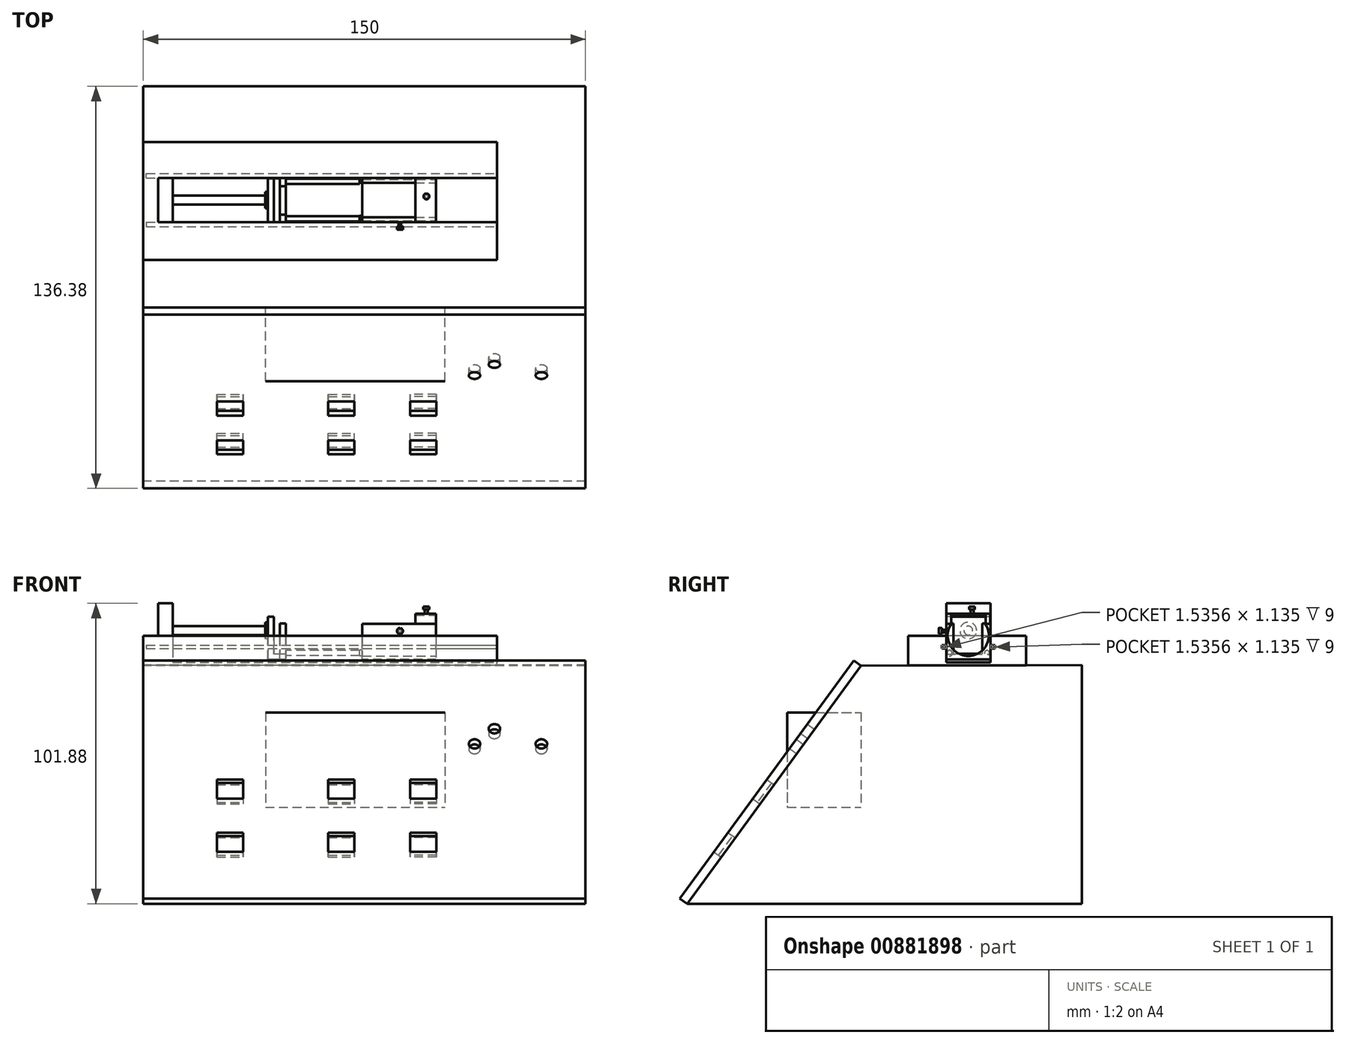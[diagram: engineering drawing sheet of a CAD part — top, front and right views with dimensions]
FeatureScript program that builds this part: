
annotation { "Feature Type Name" : "Feature", "Feature Type Description" : "" }
export const myFeature = defineFeature(function(context is Context, id is Id, definition is map)
    precondition{}
    {
        {
            var Q0;
            Q0=qCreatedBy(makeId("Right.planeOp"),FACE);
            var sketch = newSketch(context, id + "F0", { "sketchPlane" : qUnion([Q0])});
            skLineSegment(sketch, "E0", {"start": v(0, 80.75) * mm, "end": v(-58.99, 0) * mm});
            skLineSegment(sketch, "E1", {"start": v(-58.99, 0) * mm, "end": v(74.97, 0) * mm});
            skLineSegment(sketch, "E2", {"start": v(74.97, 0) * mm, "end": v(74.97, 80.92) * mm});
            skLineSegment(sketch, "E3", {"start": v(74.97, 80.92) * mm, "end": v(0, 80.75) * mm});
            skSolve(sketch);
        }
        {
            var Q0;
            Q0 = qSketchRegion(id + "F0", true);
            extrude(context, id + "F1", {"entities" : qUnion([Q0]), "depth" : 150 * mm, "offsetDistance" : 25 * mm});
        }
        {
            var Q0;
            Q0=makeQuery(id+"F1.opExtrude","CAP_FACE",FACE,{"disambiguationData":[OSD([sQuery(id+"F0.wireOp",EDGE,"E0"),sQuery(id+"F0.wireOp",EDGE,"E1"),sQuery(id+"F0.wireOp",EDGE,"E2"),sQuery(id+"F0.wireOp",EDGE,"E3")])],"isStart":true});
            var sketch = newSketch(context, id + "F2", { "sketchPlane" : qUnion([Q0])});
            skLineSegment(sketch, "E4.bottom", {"start": v(-56.05, 80.88) * mm, "end": v(-16.05, 80.88) * mm});
            skLineSegment(sketch, "E4.top", {"start": v(-56.05, 90.88) * mm, "end": v(-16.05, 90.88) * mm});
            skLineSegment(sketch, "E4.left", {"start": v(-56.05, 80.88) * mm, "end": v(-56.05, 90.88) * mm});
            skLineSegment(sketch, "E4.right", {"start": v(-16.05, 80.88) * mm, "end": v(-16.05, 90.88) * mm});
            skSolve(sketch);
        }
        {
            var Q0;
            Q0 = qSketchRegion(id + "F2", true);
            extrude(context, id + "F3", {"entities" : qUnion([Q0]), "oppositeDirection" : true, "depth" : 120 * mm, "offsetDistance" : 25 * mm});
        }
        {
            var Q0;
            Q0=makeQuery(id+"F3.opExtrude","CAP_FACE",FACE,{"disambiguationData":[OSD([sQuery(id+"F2.wireOp",EDGE,"E4.bottom"),sQuery(id+"F2.wireOp",EDGE,"E4.top"),sQuery(id+"F2.wireOp",EDGE,"E4.left"),sQuery(id+"F2.wireOp",EDGE,"E4.right")])],"isStart":false});
            var sketch = newSketch(context, id + "F4", { "sketchPlane" : qUnion([Q0])});
            skLineSegment(sketch, "E5.bottom", {"start": v(28.9, 90.88) * mm, "end": v(43.9, 90.88) * mm});
            skLineSegment(sketch, "E5.top", {"start": v(28.9, 81.88) * mm, "end": v(43.9, 81.88) * mm});
            skLineSegment(sketch, "E5.left", {"start": v(28.9, 90.88) * mm, "end": v(28.9, 81.88) * mm});
            skLineSegment(sketch, "E5.right", {"start": v(43.9, 90.88) * mm, "end": v(43.9, 81.88) * mm});
            skSolve(sketch);
        }
        {
            var Q0;
            Q0 = qSketchRegion(id + "F4", true);
            extrude(context, id + "F5", {"entities" : qUnion([Q0]), "operationType" : NewBodyOperationType.REMOVE, "oppositeDirection" : true, "depth" : 115 * mm, "offsetDistance" : 25 * mm});
        }
        {
            var Q0;
            Q0=makeQuery(id+"F5.boolean.opBoolean","COPY",FACE,{"derivedFrom":makeQuery(id+"F5.opExtrude","CAP_FACE",FACE,{"disambiguationData":[OSD([sQuery(id+"F4.wireOp",EDGE,"E5.bottom"),sQuery(id+"F4.wireOp",EDGE,"E5.top"),sQuery(id+"F4.wireOp",EDGE,"E5.left"),sQuery(id+"F4.wireOp",EDGE,"E5.right")])],"isStart":false})});
            var sketch = newSketch(context, id + "F6", { "sketchPlane" : qUnion([Q0])});
            skLineSegment(sketch, "E6.bottom", {"start": v(28.9, 81.88) * mm, "end": v(43.9, 81.88) * mm});
            skLineSegment(sketch, "E6.top", {"start": v(28.9, 101.88) * mm, "end": v(43.9, 101.88) * mm});
            skLineSegment(sketch, "E6.left", {"start": v(28.9, 81.88) * mm, "end": v(28.9, 101.88) * mm});
            skLineSegment(sketch, "E6.right", {"start": v(43.9, 81.88) * mm, "end": v(43.9, 101.88) * mm});
            skSolve(sketch);
        }
        {
            var Q0;
            Q0 = qSketchRegion(id + "F6", true);
            extrude(context, id + "F7", {"entities" : qUnion([Q0]), "operationType" : NewBodyOperationType.ADD, "depth" : 5 * mm, "offsetDistance" : 25 * mm});
        }
        {
            var Q0;
            Q0=makeQuery(id+"F7.opExtrude","CAP_FACE",FACE,{"disambiguationData":[OSD([sQuery(id+"F6.wireOp",EDGE,"E6.bottom"),sQuery(id+"F6.wireOp",EDGE,"E6.top"),sQuery(id+"F6.wireOp",EDGE,"E6.left"),sQuery(id+"F6.wireOp",EDGE,"E6.right")])],"isStart":false});
            var sketch = newSketch(context, id + "F8", { "sketchPlane" : qUnion([Q0])});
            skCircle(sketch, "E7", {"center": v(36.4, 92.68) * mm, "radius": 1.5 * mm});
            skSolve(sketch);
        }
        {
            var Q0;
            Q0 = qSketchRegion(id + "F8", true);
            extrude(context, id + "F9", {"entities" : qUnion([Q0]), "operationType" : NewBodyOperationType.ADD, "depth" : 31.3 * mm, "offsetDistance" : 25 * mm});
        }
        {
            var Q0;
            Q0=makeQuery(id+"F9.opExtrude","CAP_FACE",FACE,{"disambiguationData":[OSD([sQuery(id+"F8.wireOp",EDGE,"E7")])],"isStart":false});
            var sketch = newSketch(context, id + "F10", { "sketchPlane" : qUnion([Q0])});
            skCircle(sketch, "E8", {"center": v(36.4, 92.68) * mm, "radius": 2.83 * mm});
            skSolve(sketch);
        }
        {
            var Q0;
            Q0 = qSketchRegion(id + "F10", true);
            extrude(context, id + "F11", {"entities" : qUnion([Q0]), "operationType" : NewBodyOperationType.ADD, "depth" : 1 * mm, "offsetDistance" : 25 * mm});
        }
        {
            var Q0;
            Q0=makeQuery(id+"F11.opExtrude","CAP_FACE",FACE,{"disambiguationData":[OSD([sQuery(id+"F10.wireOp",EDGE,"E8")])],"isStart":false});
            var sketch = newSketch(context, id + "F12", { "sketchPlane" : qUnion([Q0])});
            skLineSegment(sketch, "E9", {"start": v(28.96, 82.93) * mm, "end": v(43.82, 82.93) * mm});
            skLineSegment(sketch, "E10", {"start": v(43.82, 82.93) * mm, "end": v(43.82, 97.32) * mm});
            skLineSegment(sketch, "E11", {"start": v(43.82, 97.32) * mm, "end": v(28.96, 97.32) * mm});
            skLineSegment(sketch, "E12", {"start": v(28.96, 97.32) * mm, "end": v(28.96, 82.93) * mm});
            skSolve(sketch);
        }
        {
            var Q0;
            Q0 = qSketchRegion(id + "F12", true);
            extrude(context, id + "F13", {"entities" : qUnion([Q0]), "operationType" : NewBodyOperationType.ADD, "depth" : 2 * mm, "offsetDistance" : 25 * mm});
        }
        {
            var Q0;
            Q0=makeQuery(id+"F13.opExtrude","CAP_FACE",FACE,{"disambiguationData":[OSD([sQuery(id+"F12.wireOp",EDGE,"E9"),sQuery(id+"F12.wireOp",EDGE,"E10"),sQuery(id+"F12.wireOp",EDGE,"E11"),sQuery(id+"F12.wireOp",EDGE,"E12")])],"isStart":false});
            var sketch = newSketch(context, id + "F14", { "sketchPlane" : qUnion([Q0])});
            skLineSegment(sketch, "E13.bottom", {"start": v(28.96, 82.93) * mm, "end": v(43.82, 82.93) * mm});
            skLineSegment(sketch, "E13.top", {"start": v(28.96, 84.65) * mm, "end": v(43.82, 84.65) * mm});
            skLineSegment(sketch, "E13.left", {"start": v(28.96, 82.93) * mm, "end": v(28.96, 84.65) * mm});
            skLineSegment(sketch, "E13.right", {"start": v(43.82, 82.93) * mm, "end": v(43.82, 84.65) * mm});
            skSolve(sketch);
        }
        {
            var Q0;
            Q0=makeQuery(id+"F14.imprint","IMPRINT",FACE,{"disambiguationData":[TD([[makeQuery(id+"F14.imprint","IMPRINT",EDGE,{"derivedFrom":sQuery(id+"F14.wireOp",EDGE,"E13.bottom")}),1.0]])]});
            extrude(context, id + "F15", {"entities" : qUnion([Q0]), "operationType" : NewBodyOperationType.ADD, "depth" : 2 * mm, "offsetDistance" : 25 * mm});
        }
        {
            var Q0;
            Q0=makeQuery(id+"F15.opExtrude","CAP_FACE",FACE,{"disambiguationData":[OSD([sQuery(id+"F14.wireOp",EDGE,"E13.bottom"),sQuery(id+"F14.wireOp",EDGE,"E13.top"),sQuery(id+"F14.wireOp",EDGE,"E13.left"),sQuery(id+"F14.wireOp",EDGE,"E13.right")])],"isStart":false});
            var sketch = newSketch(context, id + "F16", { "sketchPlane" : qUnion([Q0])});
            skLineSegment(sketch, "E14.bottom", {"start": v(28.96, 82.93) * mm, "end": v(43.85, 82.93) * mm});
            skLineSegment(sketch, "E14.top", {"start": v(28.96, 95.1) * mm, "end": v(43.85, 95.1) * mm});
            skLineSegment(sketch, "E14.left", {"start": v(28.96, 82.93) * mm, "end": v(28.96, 95.1) * mm});
            skLineSegment(sketch, "E14.right", {"start": v(43.85, 82.93) * mm, "end": v(43.85, 95.1) * mm});
            skSolve(sketch);
        }
        {
            var Q0;
            Q0 = qSketchRegion(id + "F16", true);
            extrude(context, id + "F17", {"entities" : qUnion([Q0]), "operationType" : NewBodyOperationType.ADD, "depth" : 2 * mm, "offsetDistance" : 25 * mm});
        }
        {
            var Q0;
            Q0=makeQuery(id+"F17.opExtrude","CAP_FACE",FACE,{"disambiguationData":[OSD([sQuery(id+"F16.wireOp",EDGE,"E14.bottom"),sQuery(id+"F16.wireOp",EDGE,"E14.top"),sQuery(id+"F16.wireOp",EDGE,"E14.left"),sQuery(id+"F16.wireOp",EDGE,"E14.right")])],"isStart":false});
            var sketch = newSketch(context, id + "F18", { "sketchPlane" : qUnion([Q0])});
            skLineSegment(sketch, "E15.bottom", {"start": v(31.42, 95.1) * mm, "end": v(41.14, 95.1) * mm});
            skLineSegment(sketch, "E15.top", {"start": v(31.42, 84.76) * mm, "end": v(41.14, 84.76) * mm});
            skLineSegment(sketch, "E15.left", {"start": v(31.42, 95.1) * mm, "end": v(31.42, 84.76) * mm});
            skLineSegment(sketch, "E15.right", {"start": v(41.14, 95.1) * mm, "end": v(41.14, 84.76) * mm});
            skSolve(sketch);
        }
        {
            var Q0;
            Q0 = qSketchRegion(id + "F18", true);
            extrude(context, id + "F19", {"entities" : qUnion([Q0]), "operationType" : NewBodyOperationType.REMOVE, "oppositeDirection" : true, "depth" : 2 * mm, "offsetDistance" : 25 * mm});
        }
        {
            var Q0;
            Q0=makeQuery(id+"F3.opExtrude","CAP_FACE",FACE,{"disambiguationData":[OSD([sQuery(id+"F2.wireOp",EDGE,"E4.bottom"),sQuery(id+"F2.wireOp",EDGE,"E4.top"),sQuery(id+"F2.wireOp",EDGE,"E4.left"),sQuery(id+"F2.wireOp",EDGE,"E4.right")])],"isStart":false});
            var sketch = newSketch(context, id + "F20", { "sketchPlane" : qUnion([Q0])});
            skLineSegment(sketch, "E16.bottom", {"start": v(43.9, 87.7) * mm, "end": v(45.44, 87.7) * mm});
            skLineSegment(sketch, "E16.top", {"start": v(43.9, 86.56) * mm, "end": v(45.44, 86.56) * mm});
            skLineSegment(sketch, "E16.left", {"start": v(43.9, 87.7) * mm, "end": v(43.9, 86.56) * mm});
            skLineSegment(sketch, "E16.right", {"start": v(45.44, 87.7) * mm, "end": v(45.44, 86.56) * mm});
            skLineSegment(sketch, "E17", {"start": v(36.4, 81.88) * mm, "end": v(36.4, 97.63) * mm});
            skLineSegment(sketch, "E18.MirrorCS", {"start": v(28.9, 87.7) * mm, "end": v(27.37, 87.7) * mm});
            skLineSegment(sketch, "E19.MirrorCS", {"start": v(27.37, 87.7) * mm, "end": v(27.37, 86.56) * mm});
            skLineSegment(sketch, "E20.MirrorCS", {"start": v(28.9, 86.56) * mm, "end": v(27.37, 86.56) * mm});
            skLineSegment(sketch, "E21.MirrorCS", {"start": v(28.9, 87.7) * mm, "end": v(28.9, 86.56) * mm});
            skSolve(sketch);
        }
        {
            var Q0;
            Q0=makeQuery(id+"F20.imprint","IMPRINT",FACE,{"disambiguationData":[TD([[makeQuery(id+"F20.imprint","IMPRINT",EDGE,{"derivedFrom":sQuery(id+"F20.wireOp",EDGE,"E16.bottom")}),-1.0]])]});
            var Q1;
            Q1=makeQuery(id+"F20.imprint","IMPRINT",FACE,{"disambiguationData":[TD([[makeQuery(id+"F20.imprint","IMPRINT",EDGE,{"derivedFrom":sQuery(id+"F20.wireOp",EDGE,"E18.MirrorCS")}),1.0]])]});
            extrude(context, id + "F21", {"entities" : qUnion([Q0, Q1]), "operationType" : NewBodyOperationType.REMOVE, "oppositeDirection" : true, "depth" : 119 * mm, "offsetDistance" : 25 * mm});
        }
        {
            var Q0;
            Q0=qCreatedBy(makeId("Front.planeOp"),FACE);
            var sketch = newSketch(context, id + "F22", { "sketchPlane" : qUnion([Q0])});
            skLineSegment(sketch, "E22.bottom", {"start": v(41.44, 64.84) * mm, "end": v(102.33, 64.84) * mm});
            skLineSegment(sketch, "E22.top", {"start": v(41.44, 32.77) * mm, "end": v(102.33, 32.77) * mm});
            skLineSegment(sketch, "E22.left", {"start": v(41.44, 64.84) * mm, "end": v(41.44, 32.77) * mm});
            skLineSegment(sketch, "E22.right", {"start": v(102.33, 64.84) * mm, "end": v(102.33, 32.77) * mm});
            skSolve(sketch);
        }
        {
            var Q0;
            Q0 = qSketchRegion(id + "F22", true);
            extrude(context, id + "F23", {"entities" : qUnion([Q0]), "depth" : 25 * mm, "offsetDistance" : 25 * mm});
        }
        {
            var Q0;
            Q0=makeQuery(id+"F1.opExtrude","SWEPT_FACE",FACE,{"disambiguationData":[OSD([sQuery(id+"F0.wireOp",EDGE,"E0")])]});
            var sketch = newSketch(context, id + "F24", { "sketchPlane" : qUnion([Q0])});
            skPoint(sketch, "E23.firstSnap0", {"position": v(0, 15.2) * mm});
            skLineSegment(sketch, "E23.bottom", {"start": v(24.95, 15.2) * mm, "end": v(33.86, 15.2) * mm});
            skLineSegment(sketch, "E23.top", {"start": v(24.95, 7.09) * mm, "end": v(33.86, 7.09) * mm});
            skLineSegment(sketch, "E23.left", {"start": v(24.95, 15.2) * mm, "end": v(24.95, 7.09) * mm});
            skLineSegment(sketch, "E23.right", {"start": v(33.86, 15.2) * mm, "end": v(33.86, 7.09) * mm});
            skLineSegment(sketch, "E24.MirrorCS", {"start": v(24.95, -15.2) * mm, "end": v(33.86, -15.2) * mm});
            skLineSegment(sketch, "E25.MirrorCS", {"start": v(24.95, -15.2) * mm, "end": v(24.95, -7.09) * mm});
            skLineSegment(sketch, "E26.MirrorCS", {"start": v(24.95, -7.09) * mm, "end": v(33.86, -7.09) * mm});
            skLineSegment(sketch, "E27.MirrorCS", {"start": v(33.86, -15.2) * mm, "end": v(33.86, -7.09) * mm});
            skLineSegment(sketch, "E28.MirrorCS", {"start": v(99.45, 15.2) * mm, "end": v(90.54, 15.2) * mm});
            skLineSegment(sketch, "E29.MirrorCS", {"start": v(99.45, 15.2) * mm, "end": v(99.45, 7.09) * mm});
            skLineSegment(sketch, "E30.MirrorCS", {"start": v(99.45, 7.09) * mm, "end": v(90.54, 7.09) * mm});
            skLineSegment(sketch, "E31.MirrorCS", {"start": v(90.54, 15.2) * mm, "end": v(90.54, 7.09) * mm});
            skLineSegment(sketch, "E32.MirrorCS", {"start": v(99.45, -7.09) * mm, "end": v(90.54, -7.09) * mm});
            skLineSegment(sketch, "E33.MirrorCS", {"start": v(99.45, -15.2) * mm, "end": v(99.45, -7.09) * mm});
            skLineSegment(sketch, "E34.MirrorCS", {"start": v(99.45, -15.2) * mm, "end": v(90.54, -15.2) * mm});
            skLineSegment(sketch, "E35.MirrorCS", {"start": v(90.54, -15.2) * mm, "end": v(90.54, -7.09) * mm});
            skLineSegment(sketch, "E36.MirrorCS", {"start": v(62.74, 15.2) * mm, "end": v(71.65, 15.2) * mm});
            skLineSegment(sketch, "E37.MirrorCS", {"start": v(71.65, 15.2) * mm, "end": v(71.65, 7.09) * mm});
            skLineSegment(sketch, "E38.MirrorCS", {"start": v(62.74, 7.09) * mm, "end": v(71.65, 7.09) * mm});
            skLineSegment(sketch, "E39.MirrorCS", {"start": v(62.74, 15.2) * mm, "end": v(62.74, 7.09) * mm});
            skLineSegment(sketch, "E40.MirrorCS", {"start": v(62.74, -7.09) * mm, "end": v(71.65, -7.09) * mm});
            skLineSegment(sketch, "E41.MirrorCS", {"start": v(71.65, -15.2) * mm, "end": v(71.65, -7.09) * mm});
            skLineSegment(sketch, "E42.MirrorCS", {"start": v(62.74, -15.2) * mm, "end": v(62.74, -7.09) * mm});
            skLineSegment(sketch, "E43.MirrorCS", {"start": v(62.74, -15.2) * mm, "end": v(71.65, -15.2) * mm});
            skCircle(sketch, "E44", {"center": v(112.34, 36.51) * mm, "radius": 1.95 * mm});
            skCircle(sketch, "E45.MirrorC", {"center": v(112.34, 30.16) * mm, "radius": 1.95 * mm});
            skCircle(sketch, "E46.MirrorC", {"center": v(119.08, 36.51) * mm, "radius": 1.95 * mm});
            skCircle(sketch, "E47.MirrorC", {"center": v(119.08, 30.16) * mm, "radius": 1.95 * mm});
            skCircle(sketch, "E48.MirrorC", {"center": v(135.01, 36.51) * mm, "radius": 1.95 * mm});
            skCircle(sketch, "E49.MirrorC", {"center": v(135.01, 30.16) * mm, "radius": 1.95 * mm});
            skSolve(sketch);
        }
        {
            var Q0;
            Q0=makeQuery(id+"F24.imprint","IMPRINT",FACE,{"disambiguationData":[TD([[makeQuery(id+"F24.imprint","IMPRINT",EDGE,{"derivedFrom":sQuery(id+"F24.wireOp",EDGE,"E23.bottom")}),-1.0]])]});
            var Q1;
            Q1=makeQuery(id+"F24.imprint","IMPRINT",FACE,{"disambiguationData":[TD([[makeQuery(id+"F24.imprint","IMPRINT",EDGE,{"derivedFrom":sQuery(id+"F24.wireOp",EDGE,"E24.MirrorCS")}),1.0]])]});
            var Q2;
            Q2=makeQuery(id+"F24.imprint","IMPRINT",FACE,{"disambiguationData":[TD([[makeQuery(id+"F24.imprint","IMPRINT",EDGE,{"derivedFrom":sQuery(id+"F24.wireOp",EDGE,"E36.MirrorCS")}),-1.0]])]});
            var Q3;
            Q3=makeQuery(id+"F24.imprint","IMPRINT",FACE,{"disambiguationData":[TD([[makeQuery(id+"F24.imprint","IMPRINT",EDGE,{"derivedFrom":sQuery(id+"F24.wireOp",EDGE,"E40.MirrorCS")}),-1.0]])]});
            var Q4;
            Q4=makeQuery(id+"F24.imprint","IMPRINT",FACE,{"disambiguationData":[TD([[makeQuery(id+"F24.imprint","IMPRINT",EDGE,{"derivedFrom":sQuery(id+"F24.wireOp",EDGE,"E28.MirrorCS")}),1.0]])]});
            var Q5;
            Q5=makeQuery(id+"F24.imprint","IMPRINT",FACE,{"disambiguationData":[TD([[makeQuery(id+"F24.imprint","IMPRINT",EDGE,{"derivedFrom":sQuery(id+"F24.wireOp",EDGE,"E32.MirrorCS")}),1.0]])]});
            extrude(context, id + "F25", {"entities" : qUnion([Q0, Q1, Q2, Q3, Q4, Q5]), "operationType" : NewBodyOperationType.ADD, "depth" : 1 * mm, "offsetDistance" : 25 * mm});
        }
        {
            var Q0;
            Q0=makeQuery(id+"F24.imprint","IMPRINT",FACE,{"disambiguationData":[TD([[makeQuery(id+"F24.imprint","IMPRINT",EDGE,{"derivedFrom":sQuery(id+"F24.wireOp",EDGE,"E44")}),1.0]])]});
            var Q1;
            Q1=makeQuery(id+"F24.imprint","IMPRINT",FACE,{"disambiguationData":[TD([[makeQuery(id+"F24.imprint","IMPRINT",EDGE,{"derivedFrom":sQuery(id+"F24.wireOp",EDGE,"E45.MirrorC")}),-1.0]])]});
            var Q2;
            Q2=makeQuery(id+"F24.imprint","IMPRINT",FACE,{"disambiguationData":[TD([[makeQuery(id+"F24.imprint","IMPRINT",EDGE,{"derivedFrom":sQuery(id+"F24.wireOp",EDGE,"E47.MirrorC")}),1.0]])]});
            var Q3;
            Q3=makeQuery(id+"F24.imprint","IMPRINT",FACE,{"disambiguationData":[TD([[makeQuery(id+"F24.imprint","IMPRINT",EDGE,{"derivedFrom":sQuery(id+"F24.wireOp",EDGE,"E46.MirrorC")}),-1.0]])]});
            var Q4;
            Q4=makeQuery(id+"F24.imprint","IMPRINT",FACE,{"disambiguationData":[TD([[makeQuery(id+"F24.imprint","IMPRINT",EDGE,{"derivedFrom":sQuery(id+"F24.wireOp",EDGE,"E48.MirrorC")}),1.0]])]});
            var Q5;
            Q5=makeQuery(id+"F24.imprint","IMPRINT",FACE,{"disambiguationData":[TD([[makeQuery(id+"F24.imprint","IMPRINT",EDGE,{"derivedFrom":sQuery(id+"F24.wireOp",EDGE,"E49.MirrorC")}),-1.0]])]});
            extrude(context, id + "F26", {"entities" : qUnion([Q0, Q1, Q2, Q3, Q4, Q5]), "depth" : 3 * mm, "offsetDistance" : 25 * mm});
        }
        {
            var Q0;
            Q0=makeQuery(id+"F17.opExtrude","CAP_FACE",FACE,{"disambiguationData":[OSD([sQuery(id+"F16.wireOp",EDGE,"E14.bottom"),sQuery(id+"F16.wireOp",EDGE,"E14.top"),sQuery(id+"F16.wireOp",EDGE,"E14.left"),sQuery(id+"F16.wireOp",EDGE,"E14.right")])],"isStart":false});
            var sketch = newSketch(context, id + "F27", { "sketchPlane" : qUnion([Q0])});
            skCircle(sketch, "E50", {"center": v(30.07, 85.02) * mm, "radius": 0.86 * mm});
            skLineSegment(sketch, "E51", {"start": v(36.4, 82.93) * mm, "end": v(36.4, 91.23) * mm});
            skCircle(sketch, "E52.MirrorC", {"center": v(42.74, 85.02) * mm, "radius": 0.86 * mm});
            skSolve(sketch);
        }
        {
            var Q0;
            Q0 = qSketchRegion(id + "F27", true);
            extrude(context, id + "F28", {"entities" : qUnion([Q0]), "operationType" : NewBodyOperationType.ADD, "depth" : 25 * mm, "offsetDistance" : 25 * mm});
        }
        {
            var Q0;
            Q0=makeQuery(id+"F28.opExtrude","CAP_FACE",FACE,{"disambiguationData":[OSD([sQuery(id+"F27.wireOp",EDGE,"E52.MirrorC")])],"isStart":false});
            var sketch = newSketch(context, id + "F29", { "sketchPlane" : qUnion([Q0])});
            skCircle(sketch, "E53", {"center": v(30.07, 85.02) * mm, "radius": 1 * mm});
            skLineSegment(sketch, "E54", {"start": v(36.04, 82.92) * mm, "end": v(36.04, 89.53) * mm});
            skSolve(sketch);
        }
        {
            var Q0;
            Q0=makeQuery(id+"F29.imprint","IMPRINT",FACE,{"disambiguationData":[TD([[makeQuery(id+"F29.imprint","IMPRINT",EDGE,{"derivedFrom":makeQuery(id+"F28.opExtrude","CAP_EDGE",EDGE,{"disambiguationData":[OSD([sQuery(id+"F27.wireOp",EDGE,"E52.MirrorC")])],"isStart":false})}),-1.0]])]});
            var sketch = newSketch(context, id + "F30", { "sketchPlane" : qUnion([Q0])});
            skCircle(sketch, "E55", {"center": v(42.75, 85.03) * mm, "radius": 1 * mm});
            skSolve(sketch);
        }
        {
            var Q0;
            Q0 = qSketchRegion(id + "F29", true);
            var Q1;
            Q1 = qSketchRegion(id + "F30", true);
            extrude(context, id + "F31", {"entities" : qUnion([Q0, Q1]), "operationType" : NewBodyOperationType.ADD, "depth" : 1 * mm, "offsetDistance" : 25 * mm});
        }
        {
            var Q0;
            Q0=makeQuery(id+"F31.opExtrude","CAP_FACE",FACE,{"disambiguationData":[OSD([sQuery(id+"F29.wireOp",EDGE,"E53")])],"isStart":false});
            var sketch = newSketch(context, id + "F32", { "sketchPlane" : qUnion([Q0])});
            skLineSegment(sketch, "E56.bottom", {"start": v(28.92, 82.91) * mm, "end": v(43.92, 82.91) * mm});
            skLineSegment(sketch, "E56.top", {"start": v(28.92, 94.91) * mm, "end": v(43.92, 94.91) * mm});
            skLineSegment(sketch, "E56.left", {"start": v(28.92, 82.91) * mm, "end": v(28.92, 94.91) * mm});
            skLineSegment(sketch, "E56.right", {"start": v(43.92, 82.91) * mm, "end": v(43.92, 94.91) * mm});
            skSolve(sketch);
        }
        {
            var Q0;
            Q0 = qSketchRegion(id + "F32", true);
            extrude(context, id + "F33", {"entities" : qUnion([Q0]), "operationType" : NewBodyOperationType.ADD, "depth" : 25 * mm, "offsetDistance" : 25 * mm});
        }
        {
            var Q0;
            Q0=makeQuery(id+"F33.opExtrude","CAP_FACE",FACE,{"disambiguationData":[OSD([sQuery(id+"F32.wireOp",EDGE,"E56.bottom"),sQuery(id+"F32.wireOp",EDGE,"E56.top"),sQuery(id+"F32.wireOp",EDGE,"E56.left"),sQuery(id+"F32.wireOp",EDGE,"E56.right")])],"isStart":false});
            var sketch = newSketch(context, id + "F34", { "sketchPlane" : qUnion([Q0])});
            skLineSegment(sketch, "E57", {"start": v(29.83, 94.91) * mm, "end": v(43.1, 94.91) * mm});
            skCircle(sketch, "E58", {"center": v(36.4, 91.04) * mm, "radius": 7 * mm});
            skSolve(sketch);
        }
        {
            var Q0;
            Q0 = qSketchRegion(id + "F34", true);
            extrude(context, id + "F35", {"entities" : qUnion([Q0]), "operationType" : NewBodyOperationType.REMOVE, "oppositeDirection" : true, "depth" : 25 * mm, "offsetDistance" : 25 * mm});
        }
        {
            var Q0;
            Q0=makeQuery(id+"F33.opExtrude","SWEPT_FACE",FACE,{"disambiguationData":[OSD([sQuery(id+"F32.wireOp",EDGE,"E56.left")])]});
            var sketch = newSketch(context, id + "F36", { "sketchPlane" : qUnion([Q0])});
            skCircle(sketch, "E59", {"center": v(87.04, 92.5) * mm, "radius": 0.44 * mm});
            skSolve(sketch);
        }
        {
            var Q0;
            Q0 = qSketchRegion(id + "F36", true);
            extrude(context, id + "F37", {"entities" : qUnion([Q0]), "operationType" : NewBodyOperationType.ADD, "depth" : 1.5 * mm, "offsetDistance" : 25 * mm});
        }
        {
            var Q0;
            Q0=makeQuery(id+"F37.opExtrude","CAP_FACE",FACE,{"disambiguationData":[OSD([sQuery(id+"F36.wireOp",EDGE,"E59")])],"isStart":false});
            var sketch = newSketch(context, id + "F38", { "sketchPlane" : qUnion([Q0])});
            skCircle(sketch, "E60", {"center": v(87.04, 92.5) * mm, "radius": 1.03 * mm});
            skSolve(sketch);
        }
        {
            var Q0;
            Q0 = qSketchRegion(id + "F38", true);
            extrude(context, id + "F39", {"entities" : qUnion([Q0]), "operationType" : NewBodyOperationType.ADD, "depth" : 1 * mm, "offsetDistance" : 25 * mm});
        }
        {
            var Q0;
            Q0=makeQuery(id+"F39.opExtrude","CAP_FACE",FACE,{"disambiguationData":[OSD([sQuery(id+"F38.wireOp",EDGE,"E60")])],"isStart":false});
            var sketch = newSketch(context, id + "F40", { "sketchPlane" : qUnion([Q0])});
            skCircle(sketch, "E61", {"center": v(87.05, 93.53) * mm, "radius": 0.1 * mm});
            skSolve(sketch);
        }
        {
            var Q0;
            Q0=makeQuery(id+"FuygRQZiiECkmNo_9.9.F40.imprint","IMPRINT",FACE,{"disambiguationData":[TD([[makeQuery(id+"FuygRQZiiECkmNo_9.9.F40.imprint","IMPRINT",EDGE,{"derivedFrom":sQuery(id+"FuygRQZiiECkmNo_9.9.F40.wireOp",EDGE,"E61")}),1.0]])]});
            var Q1;
            Q1=makeQuery(id+"FuygRQZiiECkmNo_9.1.F40.imprint","IMPRINT",FACE,{"disambiguationData":[TD([[makeQuery(id+"FuygRQZiiECkmNo_9.1.F40.imprint","IMPRINT",EDGE,{"derivedFrom":sQuery(id+"FuygRQZiiECkmNo_9.1.F40.wireOp",EDGE,"E61")}),1.0]])]});
            var Q2;
            Q2=makeQuery(id+"FuygRQZiiECkmNo_9.2.F40.imprint","IMPRINT",FACE,{"disambiguationData":[TD([[makeQuery(id+"FuygRQZiiECkmNo_9.2.F40.imprint","IMPRINT",EDGE,{"derivedFrom":sQuery(id+"FuygRQZiiECkmNo_9.2.F40.wireOp",EDGE,"E61")}),1.0]])]});
            var Q3;
            Q3=makeQuery(id+"FuygRQZiiECkmNo_9.3.F40.imprint","IMPRINT",FACE,{"disambiguationData":[TD([[makeQuery(id+"FuygRQZiiECkmNo_9.3.F40.imprint","IMPRINT",EDGE,{"derivedFrom":sQuery(id+"FuygRQZiiECkmNo_9.3.F40.wireOp",EDGE,"E61")}),1.0]])]});
            var Q4;
            Q4=makeQuery(id+"FuygRQZiiECkmNo_9.4.F40.imprint","IMPRINT",FACE,{"disambiguationData":[TD([[makeQuery(id+"FuygRQZiiECkmNo_9.4.F40.imprint","IMPRINT",EDGE,{"derivedFrom":sQuery(id+"FuygRQZiiECkmNo_9.4.F40.wireOp",EDGE,"E61")}),1.0]])]});
            var Q5;
            Q5=makeQuery(id+"FuygRQZiiECkmNo_9.5.F40.imprint","IMPRINT",FACE,{"disambiguationData":[TD([[makeQuery(id+"FuygRQZiiECkmNo_9.5.F40.imprint","IMPRINT",EDGE,{"derivedFrom":sQuery(id+"FuygRQZiiECkmNo_9.5.F40.wireOp",EDGE,"E61")}),1.0]])]});
            var Q6;
            Q6=makeQuery(id+"FuygRQZiiECkmNo_9.6.F40.imprint","IMPRINT",FACE,{"disambiguationData":[TD([[makeQuery(id+"FuygRQZiiECkmNo_9.6.F40.imprint","IMPRINT",EDGE,{"derivedFrom":sQuery(id+"FuygRQZiiECkmNo_9.6.F40.wireOp",EDGE,"E61")}),1.0]])]});
            var Q7;
            Q7=makeQuery(id+"FuygRQZiiECkmNo_9.7.F40.imprint","IMPRINT",FACE,{"disambiguationData":[TD([[makeQuery(id+"FuygRQZiiECkmNo_9.7.F40.imprint","IMPRINT",EDGE,{"derivedFrom":sQuery(id+"FuygRQZiiECkmNo_9.7.F40.wireOp",EDGE,"E61")}),1.0]])]});
            var Q8;
            Q8=makeQuery(id+"FuygRQZiiECkmNo_9.8.F40.imprint","IMPRINT",FACE,{"disambiguationData":[TD([[makeQuery(id+"FuygRQZiiECkmNo_9.8.F40.imprint","IMPRINT",EDGE,{"derivedFrom":sQuery(id+"FuygRQZiiECkmNo_9.8.F40.wireOp",EDGE,"E61")}),1.0]])]});
            var Q9;
            {var subQ0=sQuery(id+"F40.wireOp",EDGE,"E61");var subQ1=makeQuery(id+"F39.opExtrude","CAP_EDGE",EDGE,{"disambiguationData":[OSD([sQuery(id+"F38.wireOp",EDGE,"E60")])],"isStart":false});var subQ2=makeQuery(id+"F40.imprint","INTERSECT",VERTEX,{"disambiguationData":[OD(0.0)],"derivedFrom":[subQ1,subQ0]});Q9=makeQuery(id+"F40.imprint","IMPRINT",FACE,{"disambiguationData":[TD([[makeQuery(id+"F40.imprint","IMPRINT",EDGE,{"disambiguationData":[TD([[subQ2,-1.0]])],"derivedFrom":subQ0}),1.0]])]});}
            extrude(context, id + "F41", {"entities" : qUnion([Q0, Q1, Q2, Q3, Q4, Q5, Q6, Q7, Q8, Q9]), "operationType" : NewBodyOperationType.REMOVE, "oppositeDirection" : true, "depth" : 1 * mm, "offsetDistance" : 25 * mm});
        }
        {
            var Q0;
            Q0=makeQuery(id+"F33.opExtrude","CAP_FACE",FACE,{"disambiguationData":[OSD([sQuery(id+"F32.wireOp",EDGE,"E56.bottom"),sQuery(id+"F32.wireOp",EDGE,"E56.top"),sQuery(id+"F32.wireOp",EDGE,"E56.left"),sQuery(id+"F32.wireOp",EDGE,"E56.right")])],"isStart":false});
            var sketch = newSketch(context, id + "F42", { "sketchPlane" : qUnion([Q0])});
            skLineSegment(sketch, "E62.bottom", {"start": v(28.92, 94.91) * mm, "end": v(30.55, 94.91) * mm});
            skLineSegment(sketch, "E62.top", {"start": v(28.92, 97.87) * mm, "end": v(30.55, 97.87) * mm});
            skLineSegment(sketch, "E62.left", {"start": v(28.92, 94.91) * mm, "end": v(28.92, 97.87) * mm});
            skLineSegment(sketch, "E62.right", {"start": v(30.55, 94.91) * mm, "end": v(30.55, 97.87) * mm});
            skLineSegment(sketch, "E63", {"start": v(36.4, 84.04) * mm, "end": v(36.4, 98.84) * mm});
            skLineSegment(sketch, "E64.MirrorCS", {"start": v(42.24, 94.91) * mm, "end": v(42.24, 97.87) * mm});
            skLineSegment(sketch, "E65.MirrorCS", {"start": v(43.87, 97.87) * mm, "end": v(42.24, 97.87) * mm});
            skLineSegment(sketch, "E66.MirrorCS", {"start": v(43.87, 94.91) * mm, "end": v(43.87, 97.87) * mm});
            skLineSegment(sketch, "E67.MirrorCS", {"start": v(43.87, 94.91) * mm, "end": v(42.24, 94.91) * mm});
            skLineSegment(sketch, "E68.bottom", {"start": v(28.92, 97.87) * mm, "end": v(43.87, 97.87) * mm});
            skLineSegment(sketch, "E68.top", {"start": v(28.92, 98.32) * mm, "end": v(43.87, 98.32) * mm});
            skLineSegment(sketch, "E68.left", {"start": v(28.92, 97.87) * mm, "end": v(28.92, 98.32) * mm});
            skLineSegment(sketch, "E68.right", {"start": v(43.87, 97.87) * mm, "end": v(43.87, 98.32) * mm});
            skSolve(sketch);
        }
        {
            var Q0;
            Q0 = qSketchRegion(id + "F42", true);
            extrude(context, id + "F43", {"entities" : qUnion([Q0]), "oppositeDirection" : true, "depth" : 7 * mm, "offsetDistance" : 25 * mm});
        }
        {
            var Q0;
            Q0=makeQuery(id+"F43.opExtrude","SWEPT_FACE",FACE,{"disambiguationData":[OSD([sQuery(id+"F42.wireOp",EDGE,"E68.top")])]});
            var sketch = newSketch(context, id + "F44", { "sketchPlane" : qUnion([Q0])});
            skCircle(sketch, "E69", {"center": v(96.02, 37.67) * mm, "radius": 0.5 * mm});
            skSolve(sketch);
        }
        {
            var Q0;
            Q0 = qSketchRegion(id + "F44", true);
            extrude(context, id + "F45", {"entities" : qUnion([Q0]), "operationType" : NewBodyOperationType.ADD, "depth" : 1.5 * mm, "offsetDistance" : 25 * mm});
        }
        {
            var Q0;
            Q0=makeQuery(id+"F45.opExtrude","CAP_FACE",FACE,{"disambiguationData":[OSD([sQuery(id+"F44.wireOp",EDGE,"E69")])],"isStart":false});
            var sketch = newSketch(context, id + "F46", { "sketchPlane" : qUnion([Q0])});
            skCircle(sketch, "E70", {"center": v(96.02, 37.67) * mm, "radius": 1 * mm});
            skSolve(sketch);
        }
        {
            var Q0;
            Q0 = qSketchRegion(id + "F46", true);
            extrude(context, id + "F47", {"entities" : qUnion([Q0]), "operationType" : NewBodyOperationType.ADD, "depth" : 1 * mm, "offsetDistance" : 25 * mm});
        }
        {
            var Q0;
            Q0=makeQuery(id+"F47.opExtrude","CAP_FACE",FACE,{"disambiguationData":[OSD([sQuery(id+"F46.wireOp",EDGE,"E70")])],"isStart":false});
            var sketch = newSketch(context, id + "F48", { "sketchPlane" : qUnion([Q0])});
            skCircle(sketch, "E71", {"center": v(96.01, 38.67) * mm, "radius": 0.16 * mm});
            skSolve(sketch);
        }
        {
            var Q0;
            {var subQ0=sQuery(id+"F48.wireOp",EDGE,"E71");var subQ1=makeQuery(id+"F47.opExtrude","CAP_EDGE",EDGE,{"disambiguationData":[OSD([sQuery(id+"F46.wireOp",EDGE,"E70")])],"isStart":false});var subQ2=makeQuery(id+"F48.imprint","INTERSECT",VERTEX,{"disambiguationData":[OD(0.0)],"derivedFrom":[subQ1,subQ0]});Q0=makeQuery(id+"F48.imprint","IMPRINT",FACE,{"disambiguationData":[TD([[makeQuery(id+"F48.imprint","IMPRINT",EDGE,{"disambiguationData":[TD([[subQ2,-1.0]])],"derivedFrom":subQ0}),1.0]])]});}
            var Q1;
            Q1=makeQuery(id+"F0WUbSs1QCTFImB_10.1.F48.imprint","IMPRINT",FACE,{"disambiguationData":[TD([[makeQuery(id+"F0WUbSs1QCTFImB_10.1.F48.imprint","IMPRINT",EDGE,{"derivedFrom":sQuery(id+"F0WUbSs1QCTFImB_10.1.F48.wireOp",EDGE,"E71")}),1.0]])]});
            var Q2;
            Q2=makeQuery(id+"F0WUbSs1QCTFImB_10.2.F48.imprint","IMPRINT",FACE,{"disambiguationData":[TD([[makeQuery(id+"F0WUbSs1QCTFImB_10.2.F48.imprint","IMPRINT",EDGE,{"derivedFrom":sQuery(id+"F0WUbSs1QCTFImB_10.2.F48.wireOp",EDGE,"E71")}),1.0]])]});
            var Q3;
            Q3=makeQuery(id+"F0WUbSs1QCTFImB_10.3.F48.imprint","IMPRINT",FACE,{"disambiguationData":[TD([[makeQuery(id+"F0WUbSs1QCTFImB_10.3.F48.imprint","IMPRINT",EDGE,{"derivedFrom":sQuery(id+"F0WUbSs1QCTFImB_10.3.F48.wireOp",EDGE,"E71")}),1.0]])]});
            var Q4;
            Q4=makeQuery(id+"F0WUbSs1QCTFImB_10.4.F48.imprint","IMPRINT",FACE,{"disambiguationData":[TD([[makeQuery(id+"F0WUbSs1QCTFImB_10.4.F48.imprint","IMPRINT",EDGE,{"derivedFrom":sQuery(id+"F0WUbSs1QCTFImB_10.4.F48.wireOp",EDGE,"E71")}),1.0]])]});
            var Q5;
            Q5=makeQuery(id+"F0WUbSs1QCTFImB_10.5.F48.imprint","IMPRINT",FACE,{"disambiguationData":[TD([[makeQuery(id+"F0WUbSs1QCTFImB_10.5.F48.imprint","IMPRINT",EDGE,{"derivedFrom":sQuery(id+"F0WUbSs1QCTFImB_10.5.F48.wireOp",EDGE,"E71")}),1.0]])]});
            var Q6;
            Q6=makeQuery(id+"F0WUbSs1QCTFImB_10.6.F48.imprint","IMPRINT",FACE,{"disambiguationData":[TD([[makeQuery(id+"F0WUbSs1QCTFImB_10.6.F48.imprint","IMPRINT",EDGE,{"derivedFrom":sQuery(id+"F0WUbSs1QCTFImB_10.6.F48.wireOp",EDGE,"E71")}),1.0]])]});
            var Q7;
            Q7=makeQuery(id+"F0WUbSs1QCTFImB_10.7.F48.imprint","IMPRINT",FACE,{"disambiguationData":[TD([[makeQuery(id+"F0WUbSs1QCTFImB_10.7.F48.imprint","IMPRINT",EDGE,{"derivedFrom":sQuery(id+"F0WUbSs1QCTFImB_10.7.F48.wireOp",EDGE,"E71")}),1.0]])]});
            var Q8;
            Q8=makeQuery(id+"F0WUbSs1QCTFImB_10.8.F48.imprint","IMPRINT",FACE,{"disambiguationData":[TD([[makeQuery(id+"F0WUbSs1QCTFImB_10.8.F48.imprint","IMPRINT",EDGE,{"derivedFrom":sQuery(id+"F0WUbSs1QCTFImB_10.8.F48.wireOp",EDGE,"E71")}),1.0]])]});
            var Q9;
            Q9=makeQuery(id+"F0WUbSs1QCTFImB_10.9.F48.imprint","IMPRINT",FACE,{"disambiguationData":[TD([[makeQuery(id+"F0WUbSs1QCTFImB_10.9.F48.imprint","IMPRINT",EDGE,{"derivedFrom":sQuery(id+"F0WUbSs1QCTFImB_10.9.F48.wireOp",EDGE,"E71")}),1.0]])]});
            extrude(context, id + "F49", {"entities" : qUnion([Q0, Q1, Q2, Q3, Q4, Q5, Q6, Q7, Q8, Q9]), "operationType" : NewBodyOperationType.REMOVE, "oppositeDirection" : true, "depth" : 1 * mm, "offsetDistance" : 25 * mm});
        }
    });
